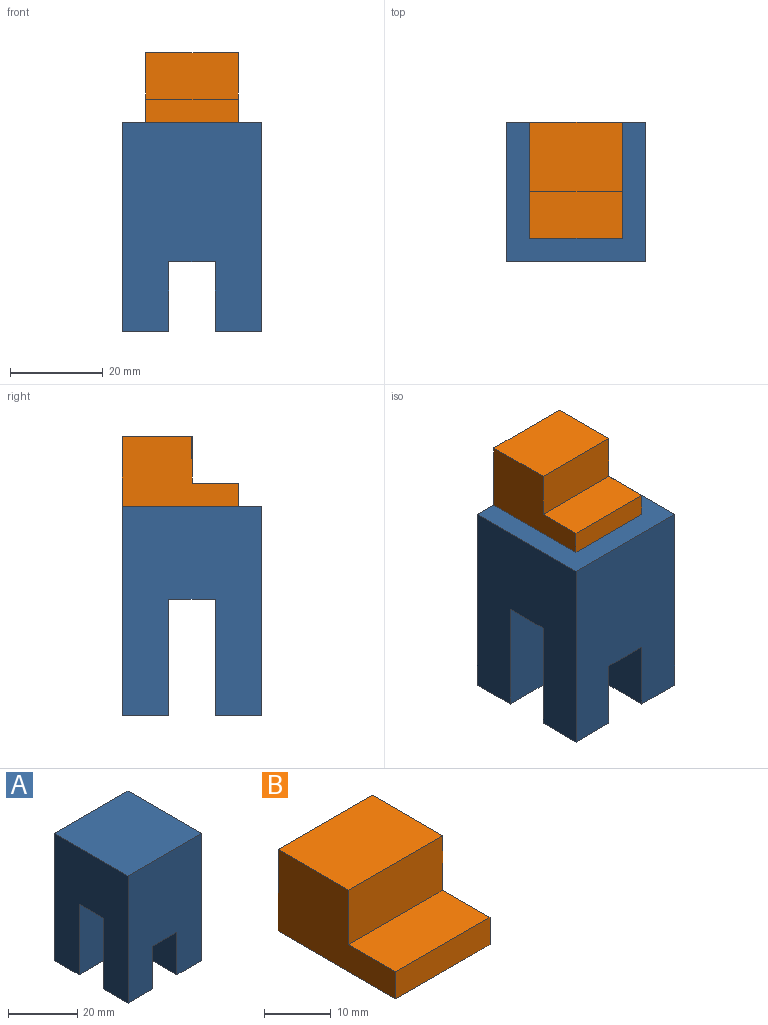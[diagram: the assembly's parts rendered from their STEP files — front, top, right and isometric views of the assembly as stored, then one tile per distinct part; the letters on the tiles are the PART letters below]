
ASSEMBLY  parts=2 mates=1
PART A: 18 faces, bbox 30x30x45 mm
  f0: plane 10x10mm, normal (0,0,-1), area 100mm2, adj f3,f11,f12,f17
  f1: plane 10x10mm, normal (0,0,-1), area 100mm2, adj f2,f11,f14,f17
  f2: plane 45x30mm, normal (-1,0,0), area 1100mm2, adj f1,f8,f9,f10,f11,f15,f16,f17
  f3: plane 45x30mm, normal (1,0,0), area 1100mm2, adj f0,f7,f8,f10,f11,f15,f16,f17
  f4: plane 15x10mm, normal (-1,0,0), area 150mm2, adj f5,f7,f10,f16
  f5: plane 10x10mm, normal (0,0,-1), area 100mm2, adj f4,f6,f10,f16
  f6: plane 15x10mm, normal (1,0,0), area 150mm2, adj f5,f9,f10,f16
  f7: plane 10x10mm, normal (0,0,-1), area 100mm2, adj f3,f4,f10,f16
  f8: plane 30x30mm, normal (0,0,1), area 900mm2, adj f2,f3,f10,f11
  f9: plane 10x10mm, normal (0,0,-1), area 100mm2, adj f2,f6,f10,f16
  f10: plane 45x30mm, normal (0,-1,0), area 1200mm2, adj f2,f3,f4,f5,f6,f7,f8,f9
  f11: plane 45x30mm, normal (0,1,0), area 1200mm2, adj f0,f1,f2,f3,f8,f12,f13,f14
  f12: plane 15x10mm, normal (-1,0,0), area 150mm2, adj f0,f11,f13,f17
  f13: plane 10x10mm, normal (0,0,-1), area 100mm2, adj f11,f12,f14,f17
  f14: plane 15x10mm, normal (1,0,0), area 150mm2, adj f1,f11,f13,f17
  f15: plane 30x10mm, normal (0,0,-1), area 300mm2, adj f2,f3,f16,f17
  f16: plane 30x25mm, normal (0,1,0), area 600mm2, adj f2,f3,f4,f5,f6,f7,f9,f15
  f17: plane 30x25mm, normal (0,-1,0), area 600mm2, adj f0,f1,f2,f3,f12,f13,f14,f15
PART B: 8 faces, bbox 20x25x15 mm
  f0: plane 20x15mm, normal (0,0,1), area 300mm2, adj f1,f5,f6,f7
  f1: plane 20x10mm, normal (0,-1,0), area 200mm2, adj f0,f2,f6,f7
  f2: plane 20x10mm, normal (0,0,1), area 200mm2, adj f1,f3,f6,f7
  f3: plane 20x5mm, normal (0,-1,0), area 100mm2, adj f2,f4,f6,f7
  f4: plane 25x20mm, normal (0,0,-1), area 500mm2, adj f3,f5,f6,f7
  f5: plane 20x15mm, normal (0,1,0), area 300mm2, adj f0,f4,f6,f7
  f6: plane 25x15mm, normal (1,0,0), area 275mm2, adj f0,f1,f2,f3,f4,f5
  f7: plane 25x15mm, normal (-1,0,0), area 275mm2, adj f0,f1,f2,f3,f4,f5
PLACE A t=(0,0,0.25)mm fixed
PLACE B t=(0,0,0.25)mm
MATE fastened B.f4 <-> A.f8  axis (0,0,-1) through (0,15,45.25)mm
